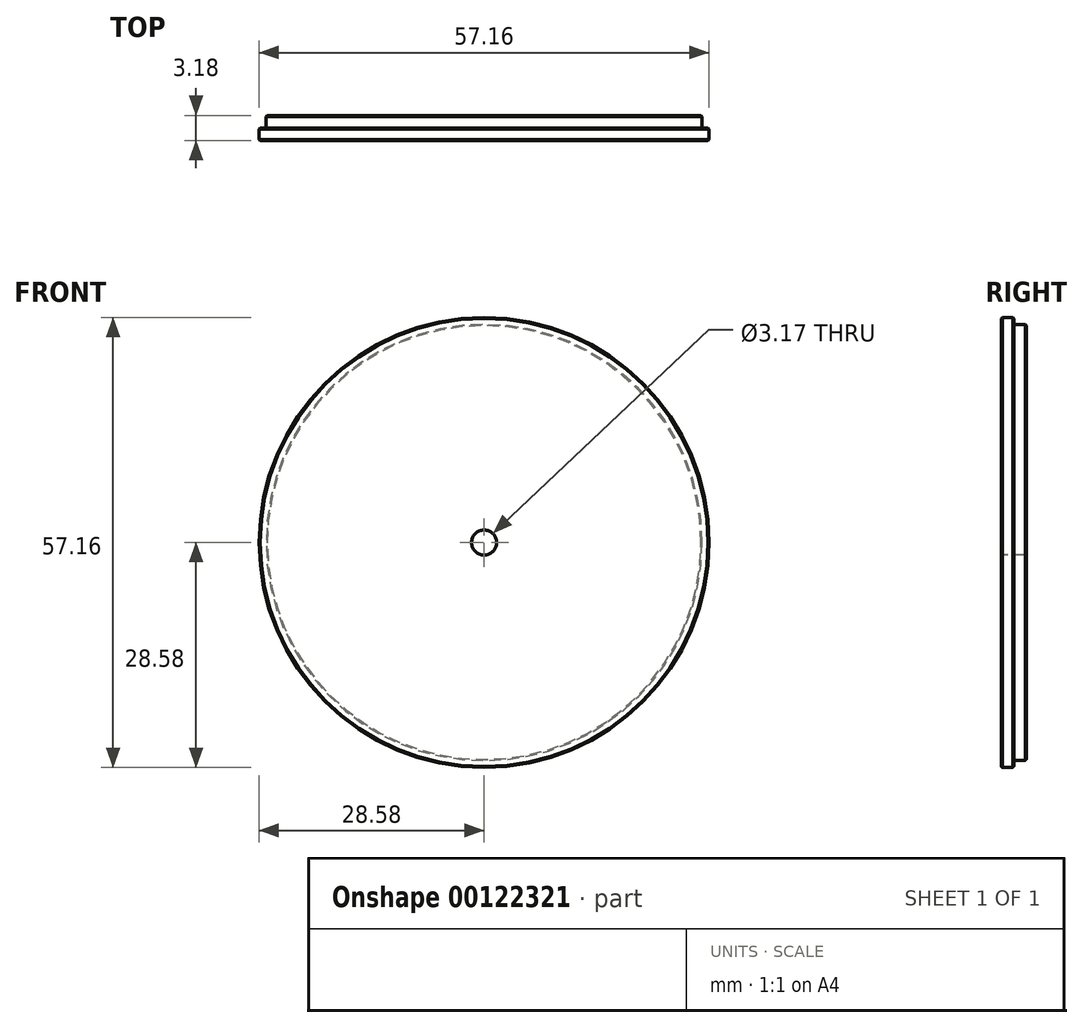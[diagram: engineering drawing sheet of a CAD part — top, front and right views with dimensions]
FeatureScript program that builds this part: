
annotation { "Feature Type Name" : "Feature", "Feature Type Description" : "" }
export const myFeature = defineFeature(function(context is Context, id is Id, definition is map)
    precondition{}
    {
        {
            var Q0;
            Q0=qCreatedBy(makeId("Front.planeOp"),FACE);
            var sketch = newSketch(context, id + "F0", { "sketchPlane" : qUnion([Q0])});
            skCircle(sketch, "E0", {"center": v(0, 0) * mm, "radius": 27.69 * mm});
            skSolve(sketch);
        }
        {
            var Q0;
            Q0=makeQuery(id+"F0.imprint","IMPRINT",FACE,{"disambiguationData":[TD([[makeQuery(id+"F0.imprint","IMPRINT",EDGE,{"derivedFrom":sQuery(id+"F0.wireOp",EDGE,"E0")}),1.0]])]});
            extrude(context, id + "F1", {"entities" : qUnion([Q0]), "depth" : 1.59 * mm});
        }
        {
            var Q0;
            Q0=makeQuery(id+"F1.opExtrude","CAP_FACE",FACE,{"disambiguationData":[OSD([sQuery(id+"F0.wireOp",EDGE,"E0")])],"isStart":false});
            var sketch = newSketch(context, id + "F2", { "sketchPlane" : qUnion([Q0])});
            skCircle(sketch, "E1", {"center": v(0, 0) * mm, "radius": 28.57 * mm});
            skSolve(sketch);
        }
        {
            var Q0;
            Q0 = qSketchRegion(id + "F2", true);
            extrude(context, id + "F3", {"entities" : qUnion([Q0]), "operationType" : NewBodyOperationType.ADD, "depth" : 1.59 * mm});
        }
        {
            var Q0;
            Q0=makeQuery(id+"F3.opExtrude","CAP_FACE",FACE,{"disambiguationData":[OSD([sQuery(id+"F2.wireOp",EDGE,"E1")])],"isStart":false});
            var sketch = newSketch(context, id + "F4", { "sketchPlane" : qUnion([Q0])});
            skCircle(sketch, "E2", {"center": v(0, 0) * mm, "radius": 1.59 * mm});
            skSolve(sketch);
        }
        {
            var Q0;
            Q0 = qSketchRegion(id + "F4", true);
            extrude(context, id + "F5", {"entities" : qUnion([Q0]), "operationType" : NewBodyOperationType.REMOVE, "endBound" : BoundingType.THROUGH_ALL, "oppositeDirection" : true, "depth" : 25.4 * mm});
        }
        {
            var Q0;
            Q0=makeQuery(id+"F3.opExtrude","CAP_EDGE",EDGE,{"disambiguationData":[OSD([sQuery(id+"F2.wireOp",EDGE,"E1")])],"isStart":false});
            var Q1;
            Q1=makeQuery(id+"F1.opExtrude","CAP_EDGE",EDGE,{"disambiguationData":[OSD([sQuery(id+"F0.wireOp",EDGE,"E0")])],"isStart":true});
            var Q2;
            Q2=makeQuery(id+"F3.opExtrude","CAP_EDGE",EDGE,{"disambiguationData":[OSD([sQuery(id+"F2.wireOp",EDGE,"E1")])],"isStart":true});
            chamfer(context, id + "F6", {"entities" : qUnion([Q0, Q1, Q2]), "width" : 0.13 * mm, "tangentPropagation" : true});
        }
    });
